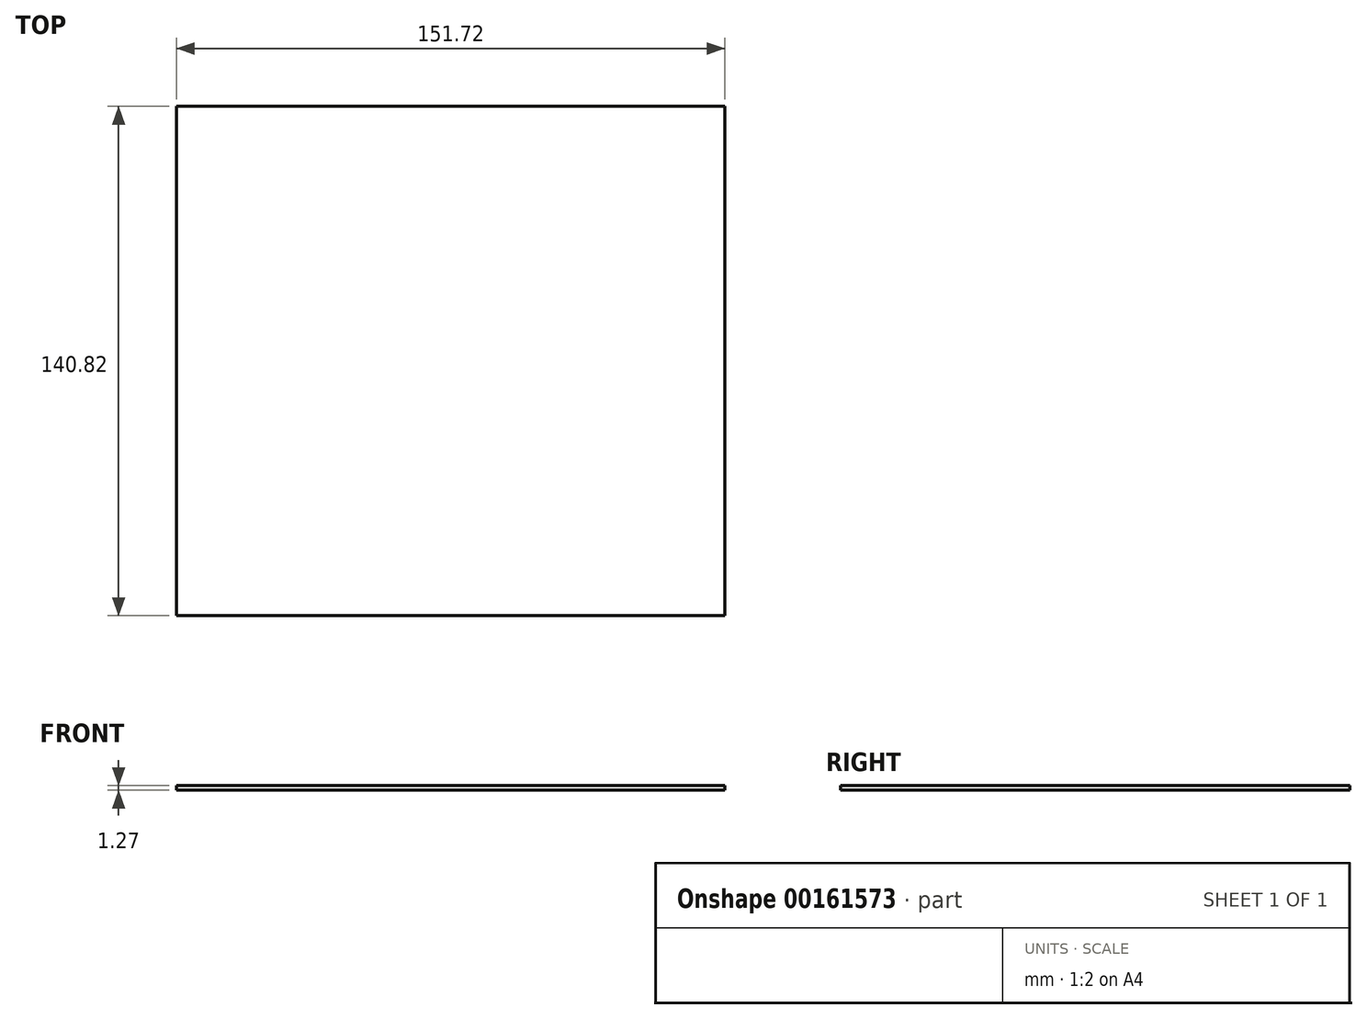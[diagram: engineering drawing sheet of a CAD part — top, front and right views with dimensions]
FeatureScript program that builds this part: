
annotation { "Feature Type Name" : "Feature", "Feature Type Description" : "" }
export const myFeature = defineFeature(function(context is Context, id is Id, definition is map)
    precondition{}
    {
        {
            var Q0;
            Q0=qCreatedBy(makeId("Top.planeOp"),FACE);
            var sketch = newSketch(context, id + "F0", { "sketchPlane" : qUnion([Q0])});
            skLineSegment(sketch, "E0.bottom", {"start": v(-86.1, 85.74) * mm, "end": v(65.63, 85.74) * mm});
            skLineSegment(sketch, "E0.top", {"start": v(-86.1, -55.08) * mm, "end": v(65.63, -55.08) * mm});
            skLineSegment(sketch, "E0.left", {"start": v(-86.1, 85.74) * mm, "end": v(-86.1, -55.08) * mm});
            skLineSegment(sketch, "E0.right", {"start": v(65.63, 85.74) * mm, "end": v(65.63, -55.08) * mm});
            skSolve(sketch);
        }
        {
            var Q0;
            Q0 = qSketchRegion(id + "F0", true);
            extrude(context, id + "F1", {"entities" : qUnion([Q0]), "depth" : 1.27 * mm});
        }
    });
